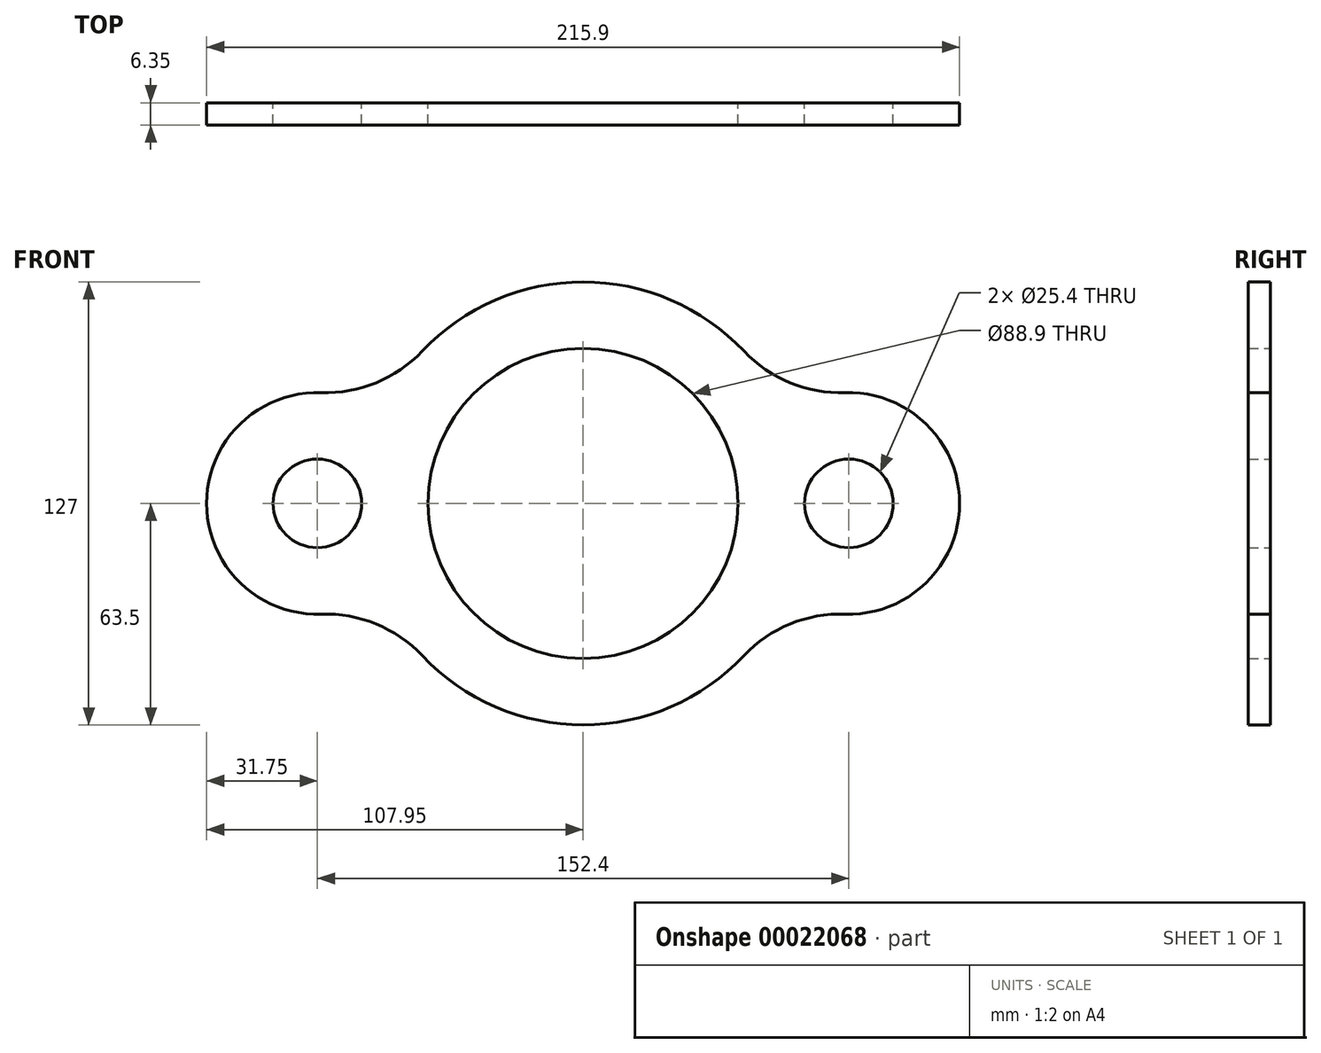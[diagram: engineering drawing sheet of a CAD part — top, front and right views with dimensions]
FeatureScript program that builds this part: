
annotation { "Feature Type Name" : "Feature", "Feature Type Description" : "" }
export const myFeature = defineFeature(function(context is Context, id is Id, definition is map)
    precondition{}
    {
        {
            var Q0;
            Q0=qCreatedBy(makeId("Front.planeOp"),FACE);
            var sketch = newSketch(context, id + "F0", { "sketchPlane" : qUnion([Q0])});
            skCircle(sketch, "E0", {"center": v(0, 0) * mm, "radius": 44.45 * mm});
            skArc(sketch, "E1", {"start": v(46.14, 43.63) * mm, "mid": v(0, 63.5) * mm, "end": v(-46.14, 43.63) * mm});
            skCircle(sketch, "E2", {"center": v(-76.2, 0) * mm, "radius": 12.7 * mm});
            skArc(sketch, "E3", {"start": v(-75.12, 31.73) * mm, "mid": v(-107.95, 0) * mm, "end": v(-75.12, -31.73) * mm});
            skCircle(sketch, "E4.MirrorC", {"center": v(76.2, 0) * mm, "radius": 12.7 * mm});
            skArc(sketch, "E5.MirrorC", {"start": v(75.12, 31.73) * mm, "mid": v(107.95, 0) * mm, "end": v(75.12, -31.73) * mm});
            skArc(sketch, "E6.trimOffspring", {"start": v(-46.14, -43.63) * mm, "mid": v(0, -63.5) * mm, "end": v(46.14, -43.63) * mm});
            skPoint(sketch, "E7.visualSharp", {"position": v(-57.94, 25.98) * mm});
            skArc(sketch, "E7.filletArc", {"start": v(-75.12, 31.73) * mm, "mid": v(-59.35, 34.56) * mm, "end": v(-46.14, 43.63) * mm});
            skPoint(sketch, "E8.visualSharp", {"position": v(57.94, 25.98) * mm});
            skArc(sketch, "E8.filletArc", {"start": v(46.14, 43.63) * mm, "mid": v(59.35, 34.56) * mm, "end": v(75.12, 31.73) * mm});
            skPoint(sketch, "E9.visualSharp", {"position": v(57.94, -25.98) * mm});
            skArc(sketch, "E9.filletArc", {"start": v(75.12, -31.73) * mm, "mid": v(59.35, -34.56) * mm, "end": v(46.14, -43.63) * mm});
            skPoint(sketch, "E10.visualSharp", {"position": v(-57.94, -25.98) * mm});
            skArc(sketch, "E10.filletArc", {"start": v(-46.14, -43.63) * mm, "mid": v(-59.35, -34.56) * mm, "end": v(-75.12, -31.73) * mm});
            skSolve(sketch);
        }
        {
            var Q0;
            Q0=makeQuery(id+"F0.imprint","IMPRINT",FACE,{"disambiguationData":[TD([[makeQuery(id+"F0.imprint","IMPRINT",EDGE,{"derivedFrom":sQuery(id+"F0.wireOp",EDGE,"E0")}),-1.0]])]});
            extrude(context, id + "F1", {"entities" : qUnion([Q0]), "depth" : 6.35 * mm});
        }
    });
